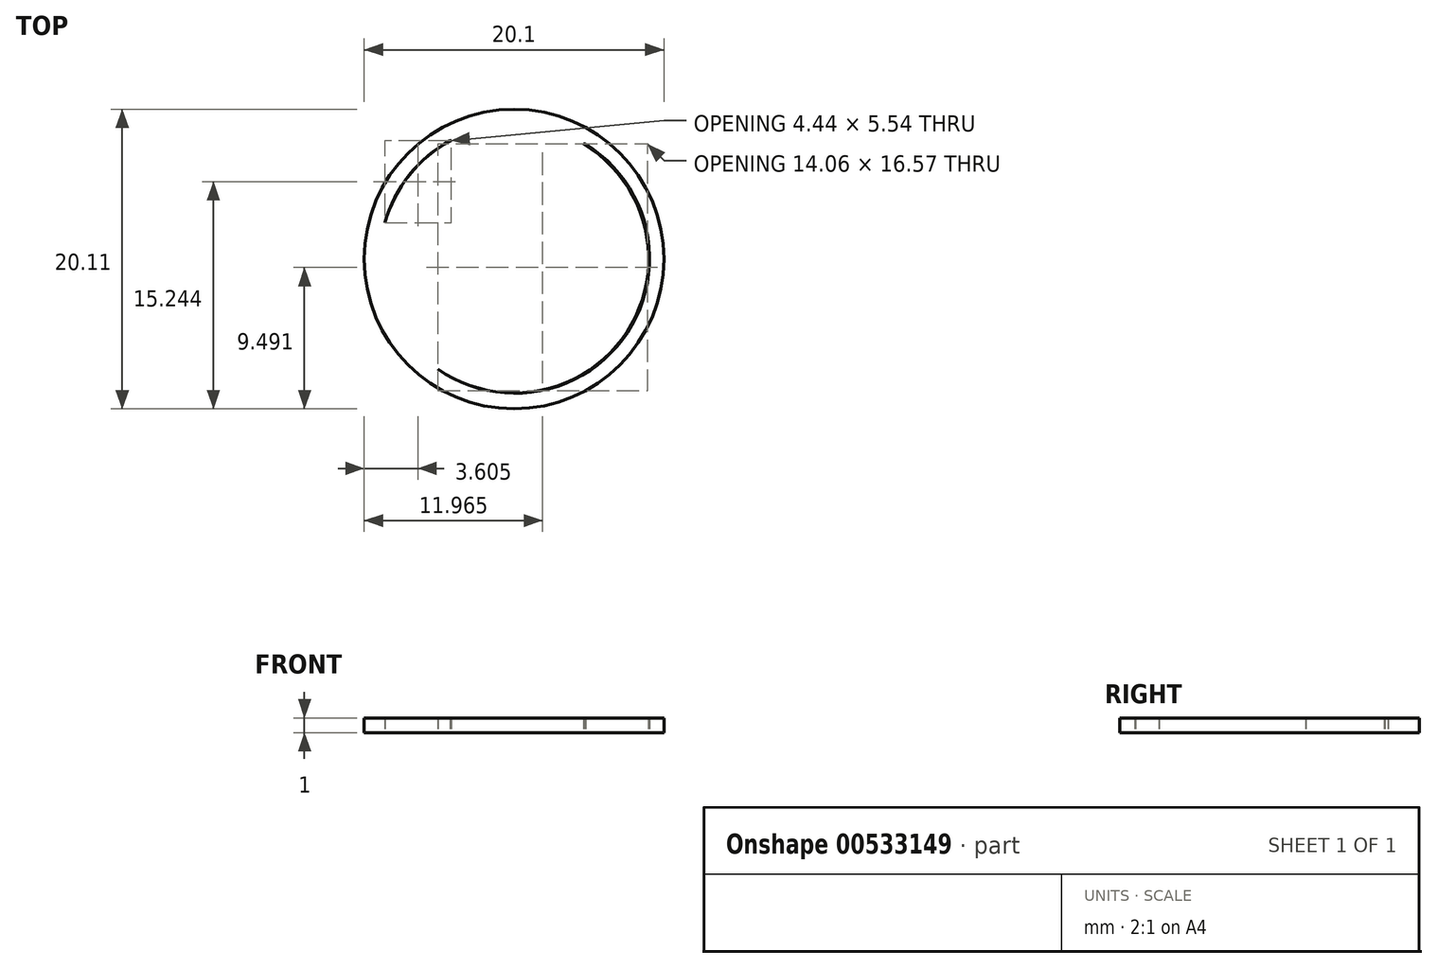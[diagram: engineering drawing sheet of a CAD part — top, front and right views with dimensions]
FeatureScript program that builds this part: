
annotation { "Feature Type Name" : "Feature", "Feature Type Description" : "" }
export const myFeature = defineFeature(function(context is Context, id is Id, definition is map)
    precondition{}
    {
        {
            var Q0;
            Q0=qCreatedBy(makeId("Top.planeOp"),FACE);
            var sketch = newSketch(context, id + "F0", { "sketchPlane" : qUnion([Q0])});
            skArc(sketch, "E0", {"start": v(-23.54, 28.74) * mm, "mid": v(-19.45, 11.77) * mm, "end": v(-14.47, 28.5) * mm});
            skLineSegment(sketch, "E1", {"start": v(-23.54, 28.74) * mm, "end": v(-14.47, 28.5) * mm});
            skSolve(sketch);
        }
        {
            var Q0;
            Q0=qCreatedBy(makeId("Top.planeOp"),FACE);
            var sketch = newSketch(context, id + "F1", { "sketchPlane" : qUnion([Q0])});
            skCircle(sketch, "E2", {"center": v(-19.26, 20.78) * mm, "radius": 10.05 * mm});
            skSolve(sketch);
        }
        {
            var Q0;
            Q0 = qSketchRegion(id + "F1", true);
            extrude(context, id + "F2", {"entities" : qUnion([Q0]), "depth" : 1 * mm, "offsetDistance" : 25.4 * mm});
        }
        {
            var Q0;
            Q0 = qSketchRegion(id + "F0", true);
            extrude(context, id + "F3", {"entities" : qUnion([Q0]), "operationType" : NewBodyOperationType.REMOVE, "depth" : 1.1 * mm, "offsetDistance" : 25.4 * mm});
        }
        {
            var Q0;
            Q0=qCreatedBy(makeId("Top.planeOp"),FACE);
            var sketch = newSketch(context, id + "F4", { "sketchPlane" : qUnion([Q0])});
            skCircle(sketch, "E3", {"center": v(-19.24, 20.8) * mm, "radius": 9 * mm});
            skSolve(sketch);
        }
        {
            var Q0;
            Q0 = qSketchRegion(id + "F4", true);
            extrude(context, id + "F5", {"entities" : qUnion([Q0]), "operationType" : NewBodyOperationType.ADD, "depth" : 1 * mm, "offsetDistance" : 25.4 * mm});
        }
    });
